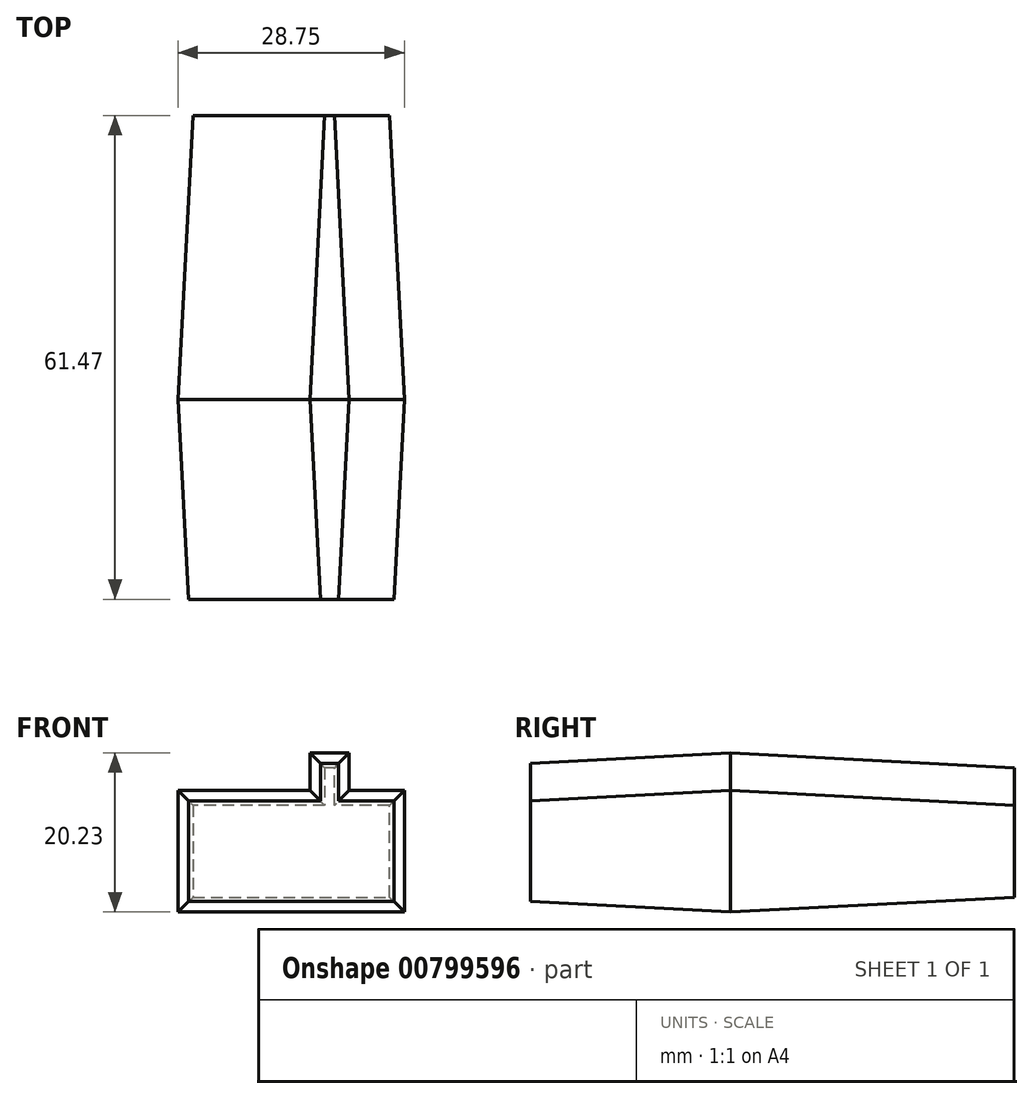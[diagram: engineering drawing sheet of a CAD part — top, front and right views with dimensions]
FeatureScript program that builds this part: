
annotation { "Feature Type Name" : "Feature", "Feature Type Description" : "" }
export const myFeature = defineFeature(function(context is Context, id is Id, definition is map)
    precondition{}
    {
        {
            var Q0;
            Q0=qCreatedBy(makeId("Front.planeOp"),FACE);
            var sketch = newSketch(context, id + "F0", { "sketchPlane" : qUnion([Q0])});
            skLineSegment(sketch, "E0.bottom", {"start": v(-7.65, 12.95) * mm, "end": v(21.1, 12.95) * mm});
            skLineSegment(sketch, "E0.top", {"start": v(-7.65, -2.5) * mm, "end": v(21.1, -2.5) * mm});
            skLineSegment(sketch, "E0.left", {"start": v(-7.65, 12.95) * mm, "end": v(-7.65, -2.5) * mm});
            skLineSegment(sketch, "E0.right", {"start": v(21.1, 12.95) * mm, "end": v(21.1, -2.5) * mm});
            skLineSegment(sketch, "E1.bottom", {"start": v(9.1, 12.95) * mm, "end": v(14.1, 12.95) * mm});
            skLineSegment(sketch, "E1.top", {"start": v(9.1, 17.73) * mm, "end": v(14.1, 17.73) * mm});
            skLineSegment(sketch, "E1.left", {"start": v(9.1, 12.95) * mm, "end": v(9.1, 17.73) * mm});
            skLineSegment(sketch, "E1.right", {"start": v(14.1, 12.95) * mm, "end": v(14.1, 17.73) * mm});
            skSolve(sketch);
        }
        {
            var Q0;
            Q0 = qSketchRegion(id + "F0", true);
            extrude(context, id + "F1", {"entities" : qUnion([Q0]), "oppositeDirection" : true, "depth" : 36.07 * mm, "offsetDistance" : 25.4 * mm, "hasDraft" : true, "draftAngle" : 3 * degree, "draftPullDirection" : true, "hasSecondDirection" : true, "secondDirectionOppositeDirection" : false, "secondDirectionDepth" : 25.4 * mm, "hasSecondDirectionDraft" : true, "secondDirectionDraftAngle" : 3 * degree, "secondDirectionDraftPullDirection" : true});
        }
    });
